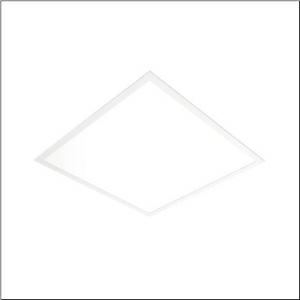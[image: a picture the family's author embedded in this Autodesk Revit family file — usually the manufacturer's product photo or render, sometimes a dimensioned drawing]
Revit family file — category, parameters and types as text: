
# Revit family: apollon_41_51mh12wm2443
name_source: partatom
category: Lighting Fixtures
units: mm (PartAtom-declared; Revit-internal decimal feet)

## family parameters
Cut with Voids When Loaded = No
Host = Face
Light Source = No
Part Type = Normal
Room Calculation Point = No
Round Connector Dimension = Use Diameter
Shared = No

## types (1)
- --- (1 x LED, 4380 lm, 35 W, 4000K)
    Apparent Load = 35 VA
    CIE Flux Codes = 61 87 97 100 100
    Color Rendering = 80
    Color Temperature = 4000K
    Default Elevation = 1800 mm
    Description = Apollon 41, office luminaire, primary optical cover: prismatic diffuser, of PS, light emission: direct distribution, primary light characteristic: symmetric, installation type: lay-in mounting, LED, rated luminous flux: 4.375lm, luminous efficacy: 125lm/W, light colour: 840, colour temperature: 4000K, control gear: ON/OFF Multilumen, with terminal, 3-pole, mains connection: 220..240V, AC, 50/60Hz, rated input power: 35W, suitable for self-contained emergency lighting element 58DB00B013A with integrated self-test function according to EN 60598-2-22, housing, of aluminium section, traffic white (RAL 9016), module: M600, length: 595mm, width: 595mm, height: 60mm, recess depth: 180mm, housing upper side, of sheet steel, protection rating (complete): IP20, protection rating (lamp compartment, on room side): IP40, insulation class (complete): insulation class II (safety insulation), certification: CE, ENEC, impact resistance: IK03, permissible operating ambient temperature: -25..+40°C, packaging unit: 1 piece
    Height = 0 mm  [stored 0 ft]
    Lamp = 1 x LED
    Lamp Light Flux = 4380 lm
    Lamp Power = 35 W
    Lamp count = 1
    Length = 600 mm
    Luminous efficacy = 125 lm/W
    Manufacturer = Siteco
    ModVariant = No
    Model = 51MH12WM2443
    Mounting Place = Ceiling
    Mounting Type = Recessed
    Number of Poles = 1
    OnlyDefault = Yes
    Power Factor = 1
    Product Name = Apollon 41
    Product group = office luminaire | ceiling recessed
    ProductGroupID = 400
    Protection Class = Protection class II
    Protection Degree = IP 20
    RLX_Detail_Level = 1
    RLX_Emergency_Light_Flux = 0 lm
    RLX_Emergency_Type = 0
    RLX_Emergency_Type_DB = No
    RlxData = <blob elided: 13125 chars, md5=d5302160>
    Socket = socket
    Standby Power = 0 W
    System Light Flux = 4380 lm
    System Power = 35 W
    Type Comments = factory setting: luminous flux: 100 % | (ON | ON) | 900 mA
    Type Image = l_1291024.jpg
    URL = http://relux.com
    VarID = @adj_033413
    Voltage = 0 V
    Weight = 0.00 kg
    Width = 600 mm

note: [stored X ft] marks values corroborated as IEEE doubles in the binary element streams (Revit-internal decimal feet)

## geometry (parser evidence)
native form markers: Sweep x10
no freeform markers — native parametric forms only
